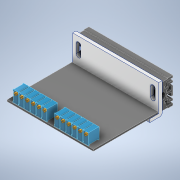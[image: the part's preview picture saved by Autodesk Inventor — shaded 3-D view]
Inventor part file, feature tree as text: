
AUTODESK INVENTOR PART (.ipt)
format: ipt  version: 2021 (Build 250183000, 183)  size: 538,624 bytes
history: native  units: mm
features: extrude x10, sketch x5, pattern_linear x2, other x2, mirror x2, projected_geometry x2, fillet x1, plane x1, boolean_combine x1
ambient origin geometry x8: Origin, YZ Plane, XZ Plane, XY Plane, X Axis, Y Axis, Z Axis, Center Point
bodies: Solid1 (feature_tree), Solid2 (feature_tree), Solid3 (feature_tree), Solid4 (feature_tree), Solid5 (feature_tree)
feature tree (26):
  sketch  "Sketch1"  dims[d0=3.0mm d1=3.0mm]
  extrude  "Extrusion1"  Depth=3.0mm
  extrude  "Extrusion2"  Depth=11.0mm
  fillet  "Fillet1"  Radius=27.0mm
  extrude  "Extrusion3"  Depth=61.0mm TaperAngle=0.0deg
  plane  "Work Plane1"
  sketch  "Sketch3"  dims[d5=77.0mm d6=0.0mm d7=61.0mm d8=0.0mm]
  extrude  "Extrusion4"  Depth=0.5mm
  sketch  "Sketch4"  dims[d9=2.0mm d10=0.5mm]
  extrude  "Extrusion7"  Depth=1.57mm TaperAngle=0.0deg
  extrude  "Extrusion8"  [1 undecoded]
  extrude  "Extrusion5"  Depth=4.8mm
  extrude  "Extrusion6"  Depth=10.0mm
  pattern_linear  "Rectangular Pattern1"  Spacing1=4.5mm  [1 undecoded]
  pattern_linear  "Rectangular Pattern2"  Spacing1=2.35mm  [1 undecoded]
  other  "Heatsink Mount"
  extrude  "Extrusion9"  Depth=1.25mm
  mirror  "Mirror1"
  boolean_combine  "Combine1"
  extrude  "Extrusion10"  Depth=1.25mm
  mirror  "Mirror2"
  sketch  "Sketch2"  dims[d2=2.0mm d3=11.0mm d4=27.0mm]
  projected_geometry  "Projected Loop1"
  projected_geometry  "Projected Loop2"
  sketch  "Sketch6"  dims[d11=58.0mm d12=1.57mm d13=0.0mm d14=-0.5mm d15=4.8mm d16=10.0mm d17=4.5mm d18=2.35mm d19=1.25mm d20=1.25mm d21=9.5mm d22=0.0mm d23=0.5mm d24=45.0deg d25=1.5mm d26=0.0mm d27=60.0mm d29=5.15mm d30=0.5mm d31=0.0mm d32=1.0mm d33=0.75mm d34=0.75mm d35=1.0mm d36=0.75mm d37=0.5mm d38=0.0mm d39=0.0mm d40=0.0mm d41=20.0mm d43=37.0mm d44=8.0mm d45=4.3mm d47=6.5mm d48=0.5mm d49=0.0mm d50=2.0mm d51=10.0mm d52=1.85mm d53=1.3mm d54=11.175mm d55=4.5mm d56=1.5mm d57=5.5mm d59=1.9mm d60=8.75mm d61=0.75mm d62=7.8mm d63=1.6mm d64=6.85mm d66=1.45mm d67=4.45mm d68=4.35mm d69=6.0mm d70=3.0mm d71=1.4mm d72=8.55mm d73=3.175mm d74=0.5mm d75=75.0mm d76=0.0mm d78=33.25mm]
  other  "Heatsink"
note: 3 required parameter values undecoded (feature->parameter linkage not recoverable at this tier; creation-order binding heuristic only, values carry confidence <= 0.55)
